# Revit family: ADB Etuve CES 505 2
name_source: partatom
category: Equipement spécialisé
units: mm (PartAtom-declared; Revit-internal decimal feet)

## family parameters
Basée sur le plan de construction = Non
Conserver l'orientation des annotations = Non
Cote de connecteur circulaire = Utiliser le diamètre
Couper avec des vides une fois chargée = Non
Partagée = Non
Repère de localisation dans la pièce = Non
Toujours verticalement = Oui
Type d'élément = Normal

## types (1)
- CES 505
    Commentaires du type = Gamme Ambassade - Fours à convection forcée
    Description = Etuve pour four CFE 505 CT
    Elévation par défaut = 0 mm  [stored 0 ft]
    Fabricant = Société Industrielle  de Lacanche
    Fréquence = 50 Hz
    Intensité nominale = 4 A
    Modèle = CES 505
    Nombres de Pôles = 1
    Phase = 1
    Poids net à vide = 54.00 kg
    Puissance électrique = 950 W
    Remarques Electricité = 230V(MONO) commutable 400V(TRI)
    Tension = 230 V
    Type de Raccord Electrique = Bornier 40A
    URL = https://www.ambassade-de-bourgogne.com

note: [stored X ft] marks values corroborated as IEEE doubles in the binary element streams (Revit-internal decimal feet)
